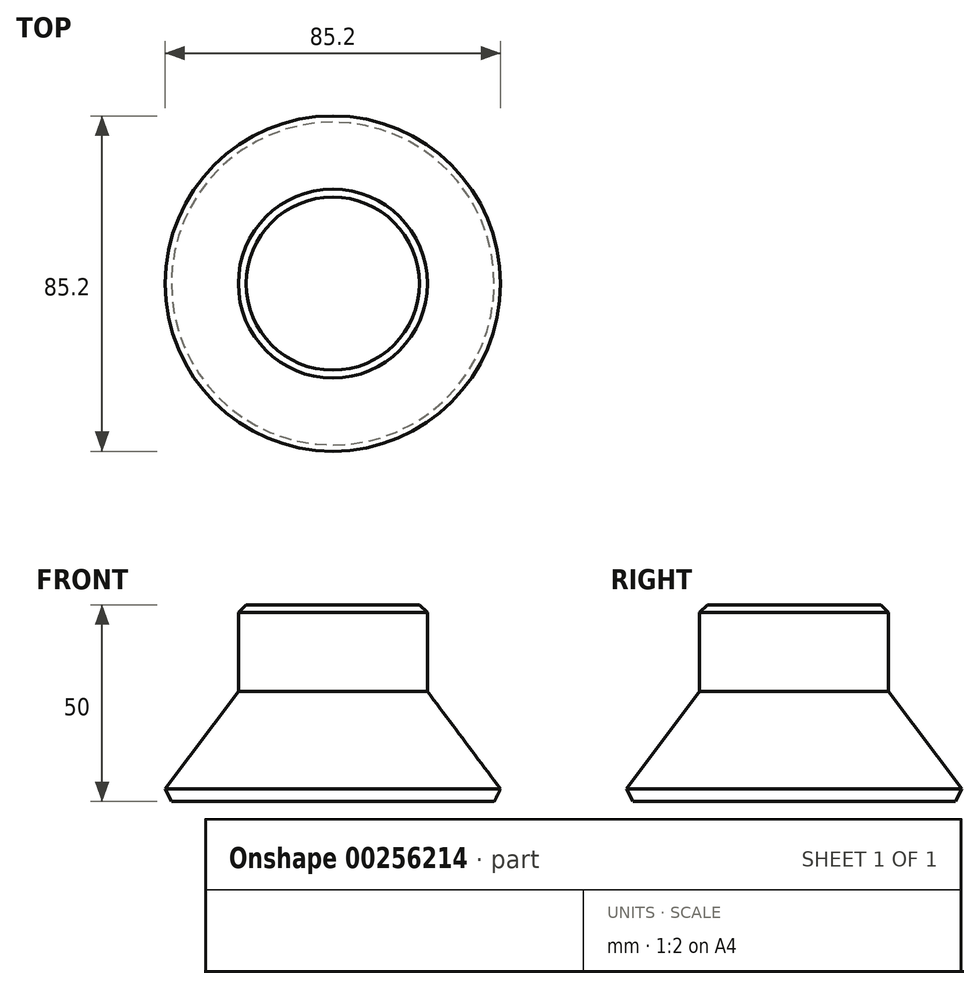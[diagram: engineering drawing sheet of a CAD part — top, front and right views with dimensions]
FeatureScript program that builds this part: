
annotation { "Feature Type Name" : "Feature", "Feature Type Description" : "" }
export const myFeature = defineFeature(function(context is Context, id is Id, definition is map)
    precondition{}
    {
        {
            var Q0;
            Q0=qCreatedBy(makeId("Right.planeOp"),FACE);
            var sketch = newSketch(context, id + "F0", { "sketchPlane" : qUnion([Q0])});
            skLineSegment(sketch, "E0", {"start": v(0, 0) * mm, "end": v(45, 0) * mm});
            skLineSegment(sketch, "E1", {"start": v(45, 0) * mm, "end": v(24, 28) * mm});
            skLineSegment(sketch, "E2", {"start": v(24, 28) * mm, "end": v(24, 50) * mm});
            skLineSegment(sketch, "E3", {"start": v(24, 50) * mm, "end": v(0, 50) * mm});
            skLineSegment(sketch, "E4", {"start": v(0, 50) * mm, "end": v(0, 0) * mm});
            skLineSegment(sketch, "E5", {"start": v(0, 66.7) * mm, "end": v(0, -48.34) * mm});
            skPoint(sketch, "E5.endSnap0", {"position": v(0, 25) * mm});
            skLineSegment(sketch, "E6", {"start": v(0, -48.34) * mm, "end": v(0, 66.7) * mm, "construction": true});
            skSolve(sketch);
        }
        {
            var Q0;
            Q0 = qSketchRegion(id + "F0", true);
            var Q1;
            Q1=sQuery(id+"F0.wireOp",EDGE,"E5");
            revolve(context, id + "F1", {"entities" : qUnion([Q0]), "axis" : qUnion([Q1]), "revolveType" : RevolveType.FULL});
        }
        {
            var Q0;
            Q0=makeQuery(id+"F1.opRevolve","SWEPT_EDGE",EDGE,{"disambiguationData":[OSD([sQuery(id+"F0.wireOp",EDGE,"E2"),sQuery(id+"F0.wireOp",EDGE,"E3")])]});
            var Q1;
            Q1=makeQuery(id+"F1.opRevolve","SWEPT_EDGE",EDGE,{"disambiguationData":[OSD([sQuery(id+"F0.wireOp",EDGE,"E0"),sQuery(id+"F0.wireOp",EDGE,"E1")])]});
            chamfer(context, id + "F2", {"entities" : qUnion([Q0, Q1]), "width" : 2 * mm, "tangentPropagation" : true});
        }
    });
